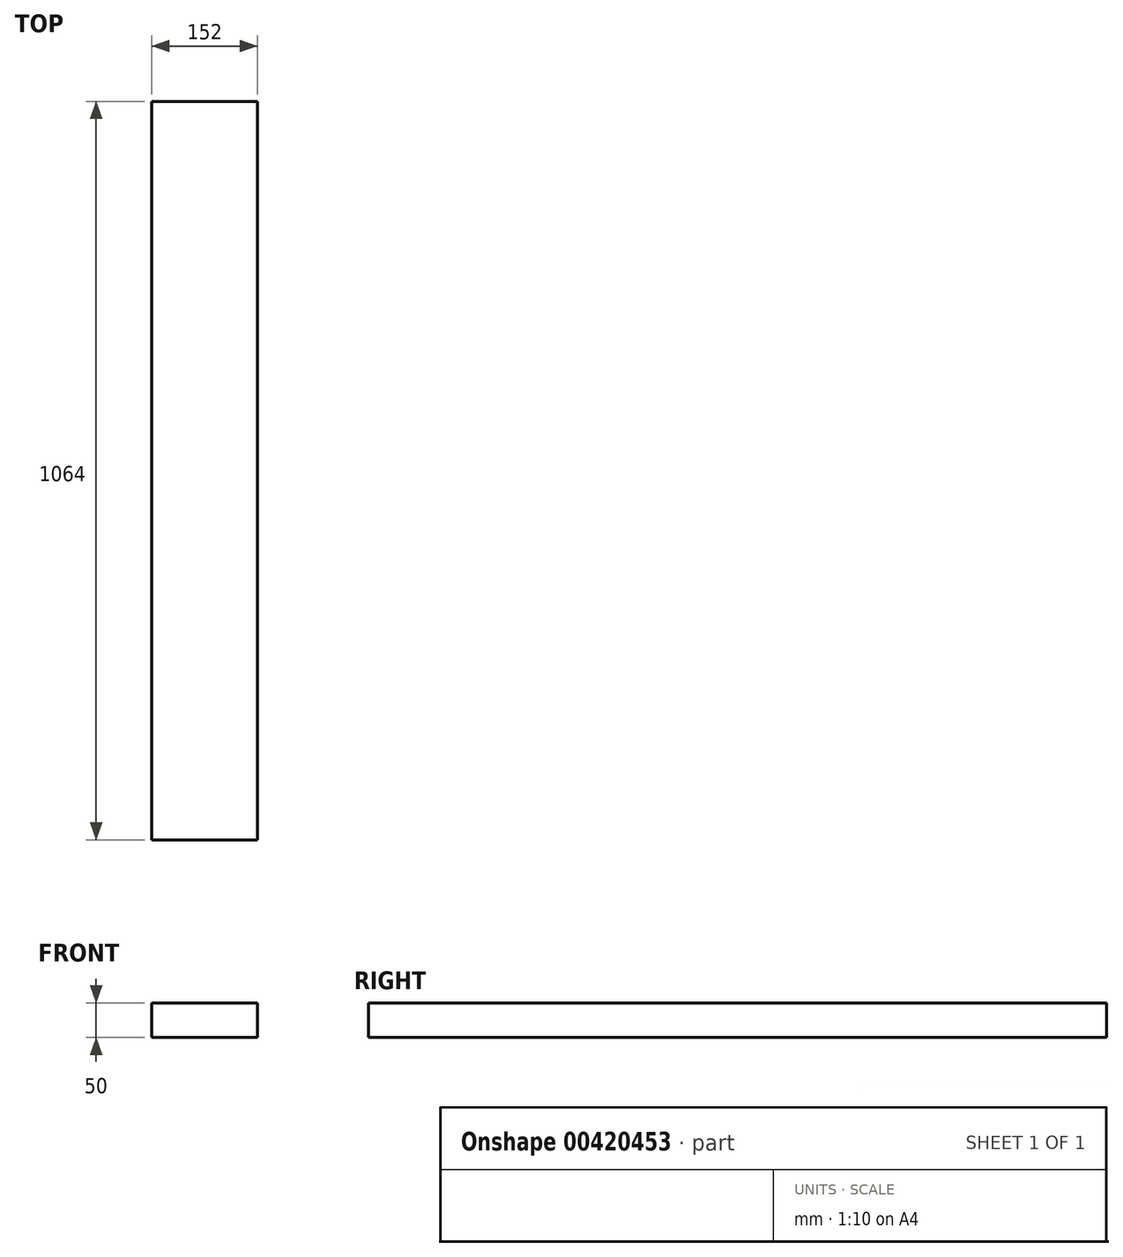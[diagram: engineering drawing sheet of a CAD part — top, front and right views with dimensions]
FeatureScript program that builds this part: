
annotation { "Feature Type Name" : "Feature", "Feature Type Description" : "" }
export const myFeature = defineFeature(function(context is Context, id is Id, definition is map)
    precondition{}
    {
        {
            var Q0;
            Q0=qCreatedBy(makeId("Front.planeOp"),FACE);
            var sketch = newSketch(context, id + "F0", { "sketchPlane" : qUnion([Q0])});
            skLineSegment(sketch, "E0.bottom", {"start": v(76, 25) * mm, "end": v(-76, 25) * mm});
            skLineSegment(sketch, "E0.top", {"start": v(76, -25) * mm, "end": v(-76, -25) * mm});
            skLineSegment(sketch, "E0.left", {"start": v(76, 25) * mm, "end": v(76, -25) * mm});
            skLineSegment(sketch, "E0.right", {"start": v(-76, 25) * mm, "end": v(-76, -25) * mm});
            skPoint(sketch, "E0.middle", {"position": v(0, 0) * mm});
            skSolve(sketch);
        }
        {
            var Q0;
            Q0=makeQuery(id+"F0.imprint","IMPRINT",FACE,{"disambiguationData":[TD([[makeQuery(id+"F0.imprint","IMPRINT",EDGE,{"derivedFrom":sQuery(id+"F0.wireOp",EDGE,"E0.bottom")}),1.0]])]});
            extrude(context, id + "F1", {"entities" : qUnion([Q0]), "endBound" : BoundingType.SYMMETRIC, "depth" : 1064 * mm});
        }
    });
